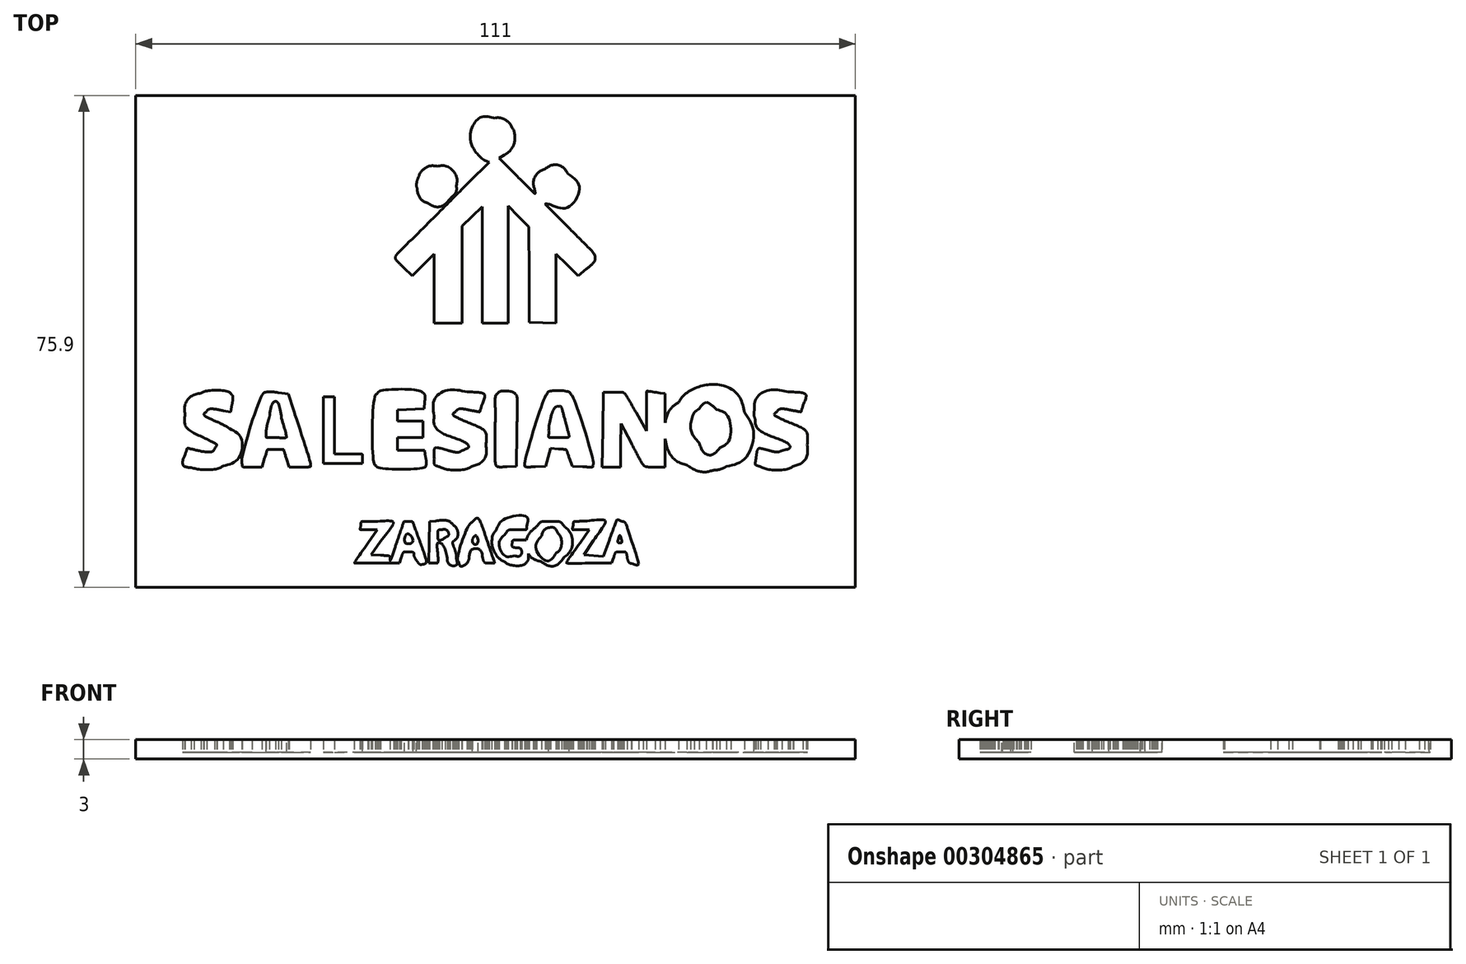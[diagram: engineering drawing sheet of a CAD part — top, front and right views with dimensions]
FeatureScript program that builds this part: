
annotation { "Feature Type Name" : "Feature", "Feature Type Description" : "" }
export const myFeature = defineFeature(function(context is Context, id is Id, definition is map)
    precondition{}
    {
        {
            var Q0;
            Q0=qCreatedBy(makeId("Top.planeOp"),FACE);
            var sketch = newSketch(context, id + "F0", { "sketchPlane" : qUnion([Q0])});
            skFitSpline(sketch, "E0", {"points": [v(-12.14, -33.88) * mm, v(-12.39, -33.52) * mm, v(-12.6, -33.06) * mm, v(-12.6, -32.86) * mm]});
            skFitSpline(sketch, "E1", {"points": [v(-12.6, -32.86) * mm, v(-12.6, -32.65) * mm, v(-12.94, -32.5) * mm, v(-13.42, -32.5) * mm]});
            skFitSpline(sketch, "E2", {"points": [v(-13.42, -32.5) * mm, v(-14.08, -32.5) * mm, v(-14.3, -32.67) * mm, v(-14.54, -33.36) * mm]});
            skLineSegment(sketch, "E3", {"start": v(-14.54, -33.36) * mm, "end": v(-14.84, -34.2) * mm});
            skLineSegment(sketch, "E4", {"start": v(-14.84, -34.2) * mm, "end": v(-17.99, -34.2) * mm});
            skFitSpline(sketch, "E5", {"points": [v(-17.99, -34.2) * mm, v(-21.78, -34.2) * mm, v(-21.79, -34.2) * mm, v(-19.7, -31.17) * mm]});
            skLineSegment(sketch, "E6", {"start": v(-19.7, -31.17) * mm, "end": v(-18.25, -29.08) * mm});
            skLineSegment(sketch, "E7", {"start": v(-18.25, -29.08) * mm, "end": v(-19.57, -29.08) * mm});
            skFitSpline(sketch, "E8", {"points": [v(-19.57, -29.08) * mm, v(-20.78, -29.08) * mm, v(-20.88, -29.03) * mm, v(-20.8, -28.44) * mm]});
            skFitSpline(sketch, "E9", {"points": [v(-20.8, -28.44) * mm, v(-20.71, -27.84) * mm, v(-20.57, -27.8) * mm, v(-18.58, -27.8) * mm]});
            skFitSpline(sketch, "E10", {"points": [v(-18.58, -27.8) * mm, v(-15.85, -27.8) * mm, v(-15.76, -28.1) * mm, v(-17.71, -30.86) * mm]});
            skLineSegment(sketch, "E11", {"start": v(-17.71, -30.86) * mm, "end": v(-19.17, -32.93) * mm});
            skLineSegment(sketch, "E12", {"start": v(-19.17, -32.93) * mm, "end": v(-17.73, -33.01) * mm});
            skFitSpline(sketch, "E13", {"points": [v(-17.73, -33.01) * mm, v(-16.6, -33.08) * mm, v(-16.3, -33.2) * mm, v(-16.29, -33.58) * mm]});
            skFitSpline(sketch, "E14", {"points": [v(-16.29, -33.58) * mm, v(-16.28, -33.85) * mm, v(-15.8, -32.66) * mm, v(-15.22, -30.93) * mm]});
            skFitSpline(sketch, "E15", {"points": [v(-15.22, -30.93) * mm, v(-14.27, -28.12) * mm, v(-14.1, -27.8) * mm, v(-13.48, -27.8) * mm]});
            skFitSpline(sketch, "E16", {"points": [v(-13.48, -27.8) * mm, v(-12.88, -27.8) * mm, v(-12.68, -28.12) * mm, v(-11.83, -30.49) * mm]});
            skFitSpline(sketch, "E17", {"points": [v(-11.83, -30.49) * mm, v(-10.86, -33.17) * mm, v(-10.73, -34.21) * mm, v(-11.36, -34.42) * mm]});
            skFitSpline(sketch, "E18", {"points": [v(-11.36, -34.42) * mm, v(-11.54, -34.48) * mm, v(-11.89, -34.23) * mm, v(-12.14, -33.88) * mm]});
            skFitSpline(sketch, "E19", {"points": [v(-13.8, -31.74) * mm, v(-14, -31.82) * mm, v(-13.84, -31.89) * mm, v(-13.45, -31.89) * mm]});
            skFitSpline(sketch, "E20", {"points": [v(-13.45, -31.89) * mm, v(-13.06, -31.89) * mm, v(-12.9, -31.82) * mm, v(-13.1, -31.74) * mm]});
            skFitSpline(sketch, "E21", {"points": [v(-13.73, -30.65) * mm, v(-13.73, -30.88) * mm, v(-13.6, -31.08) * mm, v(-13.46, -31.08) * mm]});
            skFitSpline(sketch, "E22", {"points": [v(-13.46, -31.08) * mm, v(-13.3, -31.08) * mm, v(-13.25, -30.88) * mm, v(-13.34, -30.65) * mm]});
            skFitSpline(sketch, "E23", {"points": [v(-5.66, -34.05) * mm, v(-5.86, -33.53) * mm, v(-4.09, -28.33) * mm, v(-3.56, -27.9) * mm]});
            skFitSpline(sketch, "E24", {"points": [v(-3.56, -27.9) * mm, v(-2.83, -27.3) * mm, v(-2.28, -28) * mm, v(-1.3, -30.8) * mm]});
            skFitSpline(sketch, "E25", {"points": [v(-1.3, -30.8) * mm, v(-0.18, -34.06) * mm, v(-0.16, -34.2) * mm, v(-1.03, -34.2) * mm]});
            skFitSpline(sketch, "E26", {"points": [v(-1.03, -34.2) * mm, v(-1.53, -34.2) * mm, v(-1.8, -33.98) * mm, v(-2.01, -33.36) * mm]});
            skFitSpline(sketch, "E27", {"points": [v(-2.01, -33.36) * mm, v(-2.43, -32.16) * mm, v(-3.67, -32.14) * mm, v(-4.08, -33.33) * mm]});
            skFitSpline(sketch, "E28", {"points": [v(-4.08, -33.33) * mm, v(-4.4, -34.23) * mm, v(-5.41, -34.7) * mm, v(-5.66, -34.05) * mm]});
            skFitSpline(sketch, "E29", {"points": [v(-3.4, -31.73) * mm, v(-3.68, -31.8) * mm, v(-3.52, -31.87) * mm, v(-3.05, -31.88) * mm]});
            skFitSpline(sketch, "E30", {"points": [v(-3.05, -31.88) * mm, v(-2.58, -31.88) * mm, v(-2.36, -31.82) * mm, v(-2.55, -31.74) * mm]});
            skLineSegment(sketch, "E31", {"start": v(-2.55, -31.74) * mm, "end": v(-2.55, -31.74) * mm});
            skFitSpline(sketch, "E32", {"points": [v(1.37, -34) * mm, v(0.82, -33.73) * mm, v(0.21, -33.18) * mm, v(0.02, -32.79) * mm]});
            skFitSpline(sketch, "E33", {"points": [v(0.02, -32.79) * mm, v(-0.48, -31.8) * mm, v(-0.43, -29.9) * mm, v(0.1, -29.14) * mm]});
            skFitSpline(sketch, "E34", {"points": [v(0.1, -29.14) * mm, v(1.25, -27.5) * mm, v(4.78, -27.05) * mm, v(4.78, -28.54) * mm]});
            skFitSpline(sketch, "E35", {"points": [v(4.78, -28.54) * mm, v(4.78, -29) * mm, v(4.56, -29.08) * mm, v(3.37, -29.08) * mm]});
            skFitSpline(sketch, "E36", {"points": [v(3.37, -29.08) * mm, v(2.24, -29.08) * mm, v(1.88, -29.2) * mm, v(1.52, -29.72) * mm]});
            skFitSpline(sketch, "E37", {"points": [v(1.52, -29.72) * mm, v(0.55, -31.1) * mm, v(1.38, -33.07) * mm, v(2.93, -33.07) * mm]});
            skFitSpline(sketch, "E38", {"points": [v(2.93, -33.07) * mm, v(3.83, -33.07) * mm, v(3.93, -32.07) * mm, v(3.05, -31.84) * mm]});
            skFitSpline(sketch, "E39", {"points": [v(3.05, -31.84) * mm, v(2.66, -31.74) * mm, v(2.49, -31.5) * mm, v(2.55, -31.17) * mm]});
            skFitSpline(sketch, "E40", {"points": [v(2.55, -31.17) * mm, v(2.63, -30.77) * mm, v(2.92, -30.65) * mm, v(3.79, -30.65) * mm]});
            skLineSegment(sketch, "E41", {"start": v(3.79, -30.65) * mm, "end": v(4.92, -30.65) * mm});
            skLineSegment(sketch, "E42", {"start": v(4.92, -30.65) * mm, "end": v(5, -32.19) * mm});
            skFitSpline(sketch, "E43", {"points": [v(5, -32.19) * mm, v(5.06, -33.03) * mm, v(5, -33.82) * mm, v(4.87, -33.95) * mm]});
            skFitSpline(sketch, "E44", {"points": [v(4.87, -33.95) * mm, v(4.33, -34.49) * mm, v(2.36, -34.52) * mm, v(1.37, -34) * mm]});
            skFitSpline(sketch, "E45", {"points": [v(0.41, -30.72) * mm, v(0.33, -30.52) * mm, v(0.27, -30.69) * mm, v(0.27, -31.08) * mm]});
            skFitSpline(sketch, "E46", {"points": [v(0.27, -31.08) * mm, v(0.27, -31.47) * mm, v(0.33, -31.63) * mm, v(0.41, -31.43) * mm]});
            skFitSpline(sketch, "E47", {"points": [v(3.43, -28.33) * mm, v(3.23, -28.25) * mm, v(2.91, -28.25) * mm, v(2.72, -28.33) * mm]});
            skFitSpline(sketch, "E48", {"points": [v(2.72, -28.33) * mm, v(2.52, -28.4) * mm, v(2.68, -28.47) * mm, v(3.07, -28.47) * mm]});
            skFitSpline(sketch, "E49", {"points": [v(7.07, -34) * mm, v(5.23, -33.06) * mm, v(4.85, -30.3) * mm, v(6.33, -28.59) * mm]});
            skFitSpline(sketch, "E50", {"points": [v(6.33, -28.59) * mm, v(6.9, -27.92) * mm, v(7.23, -27.8) * mm, v(8.48, -27.8) * mm]});
            skFitSpline(sketch, "E51", {"points": [v(8.48, -27.8) * mm, v(9.74, -27.8) * mm, v(10.05, -27.92) * mm, v(10.64, -28.6) * mm]});
            skFitSpline(sketch, "E52", {"points": [v(10.64, -28.6) * mm, v(11.67, -29.8) * mm, v(11.63, -32.17) * mm, v(10.55, -33.35) * mm]});
            skFitSpline(sketch, "E53", {"points": [v(10.55, -33.35) * mm, v(9.55, -34.45) * mm, v(8.36, -34.67) * mm, v(7.07, -34) * mm]});
            skFitSpline(sketch, "E54", {"points": [v(9.39, -32.6) * mm, v(10, -32.04) * mm, v(10.09, -30.3) * mm, v(9.54, -29.54) * mm]});
            skFitSpline(sketch, "E55", {"points": [v(9.54, -29.54) * mm, v(8.96, -28.76) * mm, v(7.58, -29.04) * mm, v(7.1, -30.03) * mm]});
            skFitSpline(sketch, "E56", {"points": [v(7.1, -30.03) * mm, v(6.2, -31.92) * mm, v(7.96, -33.9) * mm, v(9.39, -32.6) * mm]});
            skFitSpline(sketch, "E57", {"points": [v(8.14, -28.32) * mm, v(7.92, -28.41) * mm, v(7.98, -28.48) * mm, v(8.32, -28.5) * mm]});
            skFitSpline(sketch, "E58", {"points": [v(8.32, -28.5) * mm, v(8.62, -28.5) * mm, v(8.78, -28.44) * mm, v(8.69, -28.34) * mm]});
            skLineSegment(sketch, "E59", {"start": v(8.69, -28.34) * mm, "end": v(8.69, -28.34) * mm});
            skFitSpline(sketch, "E60", {"points": [v(20.96, -34.29) * mm, v(20.7, -34.22) * mm, v(20.4, -33.8) * mm, v(20.3, -33.34) * mm]});
            skFitSpline(sketch, "E61", {"points": [v(20.3, -33.34) * mm, v(20.15, -32.65) * mm, v(19.97, -32.5) * mm, v(19.3, -32.5) * mm]});
            skFitSpline(sketch, "E62", {"points": [v(19.3, -32.5) * mm, v(18.67, -32.5) * mm, v(18.44, -32.68) * mm, v(18.2, -33.36) * mm]});
            skLineSegment(sketch, "E63", {"start": v(18.2, -33.36) * mm, "end": v(17.9, -34.2) * mm});
            skLineSegment(sketch, "E64", {"start": v(17.9, -34.2) * mm, "end": v(14.76, -34.2) * mm});
            skFitSpline(sketch, "E65", {"points": [v(14.76, -34.2) * mm, v(10.96, -34.2) * mm, v(10.92, -34.14) * mm, v(13.05, -31.12) * mm]});
            skLineSegment(sketch, "E66", {"start": v(13.05, -31.12) * mm, "end": v(14.48, -29.08) * mm});
            skLineSegment(sketch, "E67", {"start": v(14.48, -29.08) * mm, "end": v(13.17, -29.08) * mm});
            skFitSpline(sketch, "E68", {"points": [v(13.17, -29.08) * mm, v(11.97, -29.08) * mm, v(11.87, -29.03) * mm, v(11.95, -28.44) * mm]});
            skFitSpline(sketch, "E69", {"points": [v(11.95, -28.44) * mm, v(12.03, -27.85) * mm, v(12.21, -27.8) * mm, v(14.11, -27.72) * mm]});
            skFitSpline(sketch, "E70", {"points": [v(14.11, -27.72) * mm, v(16.85, -27.6) * mm, v(16.94, -27.9) * mm, v(15.07, -30.73) * mm]});
            skLineSegment(sketch, "E71", {"start": v(15.07, -30.73) * mm, "end": v(13.61, -32.93) * mm});
            skLineSegment(sketch, "E72", {"start": v(13.61, -32.93) * mm, "end": v(15.1, -33.07) * mm});
            skLineSegment(sketch, "E73", {"start": v(15.1, -33.07) * mm, "end": v(16.6, -33.21) * mm});
            skLineSegment(sketch, "E74", {"start": v(16.6, -33.21) * mm, "end": v(17.54, -30.65) * mm});
            skFitSpline(sketch, "E75", {"points": [v(17.54, -30.65) * mm, v(18.6, -27.75) * mm, v(18.75, -27.53) * mm, v(19.5, -27.77) * mm]});
            skFitSpline(sketch, "E76", {"points": [v(19.5, -27.77) * mm, v(19.9, -27.9) * mm, v(20.31, -28.77) * mm, v(21.01, -30.94) * mm]});
            skFitSpline(sketch, "E77", {"points": [v(21.01, -30.94) * mm, v(21.98, -33.92) * mm, v(21.97, -34.52) * mm, v(20.96, -34.29) * mm]});
            skFitSpline(sketch, "E78", {"points": [v(18.81, -31.73) * mm, v(18.53, -31.8) * mm, v(18.7, -31.87) * mm, v(19.16, -31.88) * mm]});
            skFitSpline(sketch, "E79", {"points": [v(19.16, -31.88) * mm, v(19.63, -31.88) * mm, v(19.86, -31.82) * mm, v(19.67, -31.74) * mm]});
            skLineSegment(sketch, "E80", {"start": v(19.67, -31.74) * mm, "end": v(19.67, -31.74) * mm});
            skFitSpline(sketch, "E81", {"points": [v(19.39, -30.5) * mm, v(19.3, -30.2) * mm, v(19.2, -29.94) * mm, v(19.16, -29.94) * mm]});
            skFitSpline(sketch, "E82", {"points": [v(19.16, -29.94) * mm, v(19.12, -29.94) * mm, v(19.02, -30.2) * mm, v(18.94, -30.5) * mm]});
            skFitSpline(sketch, "E83", {"points": [v(18.94, -30.5) * mm, v(18.84, -30.86) * mm, v(18.93, -31.08) * mm, v(19.16, -31.08) * mm]});
            skFitSpline(sketch, "E84", {"points": [v(19.16, -31.08) * mm, v(19.4, -31.08) * mm, v(19.48, -30.86) * mm, v(19.39, -30.5) * mm]});
            skLineSegment(sketch, "E85", {"start": v(-10.25, -31) * mm, "end": v(-10.17, -27.8) * mm});
            skLineSegment(sketch, "E86", {"start": v(-10.17, -27.8) * mm, "end": v(-9.2, -27.7) * mm});
            skFitSpline(sketch, "E87", {"points": [v(-9.2, -27.7) * mm, v(-7.98, -27.6) * mm, v(-7.06, -27.82) * mm, v(-6.49, -28.4) * mm]});
            skFitSpline(sketch, "E88", {"points": [v(-6.49, -28.4) * mm, v(-5.97, -28.91) * mm, v(-5.9, -30.25) * mm, v(-6.36, -30.71) * mm]});
            skFitSpline(sketch, "E89", {"points": [v(-6.36, -30.71) * mm, v(-6.6, -30.95) * mm, v(-6.6, -31.27) * mm, v(-6.36, -31.95) * mm]});
            skFitSpline(sketch, "E90", {"points": [v(-6.36, -31.95) * mm, v(-6.19, -32.46) * mm, v(-6.04, -33.17) * mm, v(-6.04, -33.54) * mm]});
            skFitSpline(sketch, "E91", {"points": [v(-6.04, -33.54) * mm, v(-6.04, -34.53) * mm, v(-7.11, -34.44) * mm, v(-7.47, -33.43) * mm]});
            skFitSpline(sketch, "E92", {"points": [v(-7.47, -33.43) * mm, v(-8.21, -31.35) * mm, v(-8.9, -31.1) * mm, v(-8.9, -32.9) * mm]});
            skFitSpline(sketch, "E93", {"points": [v(-8.9, -32.9) * mm, v(-8.9, -34.11) * mm, v(-8.94, -34.2) * mm, v(-9.61, -34.2) * mm]});
            skLineSegment(sketch, "E94", {"start": v(-9.61, -34.2) * mm, "end": v(-10.33, -34.2) * mm});
            skLineSegment(sketch, "E95", {"start": v(-10.33, -34.2) * mm, "end": v(-10.25, -31) * mm});
            skFitSpline(sketch, "E96", {"points": [v(-9.54, -32.15) * mm, v(-9.61, -31.8) * mm, v(-9.67, -32.02) * mm, v(-9.67, -32.64) * mm]});
            skFitSpline(sketch, "E97", {"points": [v(-9.67, -32.64) * mm, v(-9.68, -33.27) * mm, v(-9.62, -33.56) * mm, v(-9.55, -33.29) * mm]});
            skFitSpline(sketch, "E98", {"points": [v(-9.54, -29.3) * mm, v(-9.61, -28.95) * mm, v(-9.67, -29.17) * mm, v(-9.67, -29.8) * mm]});
            skFitSpline(sketch, "E99", {"points": [v(-9.67, -29.8) * mm, v(-9.68, -30.42) * mm, v(-9.62, -30.71) * mm, v(-9.55, -30.44) * mm]});
            skFitSpline(sketch, "E100", {"points": [v(-7.78, -30.25) * mm, v(-7.23, -29.9) * mm, v(-7.6, -29.08) * mm, v(-8.31, -29.08) * mm]});
            skFitSpline(sketch, "E101", {"points": [v(-8.31, -29.08) * mm, v(-8.74, -29.08) * mm, v(-8.9, -29.27) * mm, v(-8.9, -29.8) * mm]});
            skFitSpline(sketch, "E102", {"points": [v(-8.9, -29.8) * mm, v(-8.9, -30.53) * mm, v(-8.48, -30.7) * mm, v(-7.78, -30.25) * mm]});
            skFitSpline(sketch, "E103", {"points": [v(-8.25, -28.33) * mm, v(-8.45, -28.25) * mm, v(-8.77, -28.25) * mm, v(-8.96, -28.33) * mm]});
            skFitSpline(sketch, "E104", {"points": [v(-8.96, -28.33) * mm, v(-9.16, -28.4) * mm, v(-9, -28.47) * mm, v(-8.6, -28.47) * mm]});
            skFitSpline(sketch, "E105", {"points": [v(-46.96, -19.49) * mm, v(-48.01, -19.28) * mm, v(-48.29, -18.7) * mm, v(-47.9, -17.53) * mm]});
            skFitSpline(sketch, "E106", {"points": [v(-47.9, -17.53) * mm, v(-47.57, -16.52) * mm, v(-47.52, -16.5) * mm, v(-46.52, -16.7) * mm]});
            skFitSpline(sketch, "E107", {"points": [v(-46.52, -16.7) * mm, v(-44.91, -17.04) * mm, v(-43.6, -16.97) * mm, v(-43.34, -16.54) * mm]});
            skFitSpline(sketch, "E108", {"points": [v(-43.34, -16.54) * mm, v(-43, -15.98) * mm, v(-43.2, -15.78) * mm, v(-45.05, -14.85) * mm]});
            skFitSpline(sketch, "E109", {"points": [v(-45.05, -14.85) * mm, v(-47.17, -13.78) * mm, v(-47.9, -12.86) * mm, v(-47.9, -11.27) * mm]});
            skFitSpline(sketch, "E110", {"points": [v(-47.9, -11.27) * mm, v(-47.9, -9.77) * mm, v(-46.94, -8.49) * mm, v(-45.43, -8) * mm]});
            skFitSpline(sketch, "E111", {"points": [v(-45.43, -8) * mm, v(-44.3, -7.62) * mm, v(-41.18, -7.78) * mm, v(-40.72, -8.24) * mm]});
            skFitSpline(sketch, "E112", {"points": [v(-40.72, -8.24) * mm, v(-40.56, -8.4) * mm, v(-40.53, -9.02) * mm, v(-40.64, -9.71) * mm]});
            skLineSegment(sketch, "E113", {"start": v(-40.64, -9.71) * mm, "end": v(-40.84, -10.9) * mm});
            skLineSegment(sketch, "E114", {"start": v(-40.84, -10.9) * mm, "end": v(-42.03, -10.69) * mm});
            skFitSpline(sketch, "E115", {"points": [v(-42.03, -10.69) * mm, v(-43.5, -10.43) * mm, v(-44.21, -10.46) * mm, v(-44.56, -10.82) * mm]});
            skFitSpline(sketch, "E116", {"points": [v(-44.56, -10.82) * mm, v(-45, -11.25) * mm, v(-44.56, -11.69) * mm, v(-42.97, -12.42) * mm]});
            skFitSpline(sketch, "E117", {"points": [v(-42.97, -12.42) * mm, v(-42.16, -12.8) * mm, v(-41.3, -13.27) * mm, v(-41.05, -13.47) * mm]});
            skFitSpline(sketch, "E118", {"points": [v(-41.05, -13.47) * mm, v(-39.21, -14.98) * mm, v(-39.74, -18.14) * mm, v(-42, -19.2) * mm]});
            skFitSpline(sketch, "E119", {"points": [v(-42, -19.2) * mm, v(-42.95, -19.66) * mm, v(-45.38, -19.8) * mm, v(-46.96, -19.49) * mm]});
            skFitSpline(sketch, "E120", {"points": [v(-42.21, -18.32) * mm, v(-41.17, -17.67) * mm, v(-40.8, -17.1) * mm, v(-40.8, -16.08) * mm]});
            skFitSpline(sketch, "E121", {"points": [v(-40.8, -16.08) * mm, v(-40.78, -14.88) * mm, v(-41.87, -13.62) * mm, v(-43.32, -13.14) * mm]});
            skFitSpline(sketch, "E122", {"points": [v(-43.32, -13.14) * mm, v(-45.42, -12.45) * mm, v(-46.2, -11.18) * mm, v(-45.15, -10.13) * mm]});
            skFitSpline(sketch, "E123", {"points": [v(-45.15, -10.13) * mm, v(-44.78, -9.76) * mm, v(-44.3, -9.68) * mm, v(-43.01, -9.78) * mm]});
            skFitSpline(sketch, "E124", {"points": [v(-43.01, -9.78) * mm, v(-41.58, -9.88) * mm, v(-41.36, -9.83) * mm, v(-41.36, -9.4) * mm]});
            skFitSpline(sketch, "E125", {"points": [v(-41.36, -9.4) * mm, v(-41.36, -8) * mm, v(-45.5, -8.33) * mm, v(-46.74, -9.83) * mm]});
            skFitSpline(sketch, "E126", {"points": [v(-46.74, -9.83) * mm, v(-47.28, -10.48) * mm, v(-47.2, -12.22) * mm, v(-46.58, -12.9) * mm]});
            skFitSpline(sketch, "E127", {"points": [v(-46.58, -12.9) * mm, v(-46.3, -13.22) * mm, v(-45.35, -13.8) * mm, v(-44.5, -14.18) * mm]});
            skFitSpline(sketch, "E128", {"points": [v(-44.5, -14.18) * mm, v(-42.76, -14.95) * mm, v(-42.5, -15.22) * mm, v(-42.5, -16.33) * mm]});
            skFitSpline(sketch, "E129", {"points": [v(-42.5, -16.33) * mm, v(-42.5, -17.4) * mm, v(-43.35, -17.8) * mm, v(-45.36, -17.61) * mm]});
            skFitSpline(sketch, "E130", {"points": [v(-45.36, -17.61) * mm, v(-46.8, -17.48) * mm, v(-47.02, -17.53) * mm, v(-47.14, -18) * mm]});
            skFitSpline(sketch, "E131", {"points": [v(-47.14, -18) * mm, v(-47.24, -18.4) * mm, v(-47.1, -18.59) * mm, v(-46.67, -18.68) * mm]});
            skFitSpline(sketch, "E132", {"points": [v(-46.67, -18.68) * mm, v(-46.33, -18.75) * mm, v(-45.8, -18.86) * mm, v(-45.49, -18.93) * mm]});
            skFitSpline(sketch, "E133", {"points": [v(-45.49, -18.93) * mm, v(-44.6, -19.11) * mm, v(-43, -18.82) * mm, v(-42.21, -18.32) * mm]});
            skFitSpline(sketch, "E134", {"points": [v(-8.68, -19.35) * mm, v(-9.3, -19.12) * mm, v(-9.46, -18.9) * mm, v(-9.46, -18.17) * mm]});
            skFitSpline(sketch, "E135", {"points": [v(-9.46, -18.17) * mm, v(-9.45, -16.59) * mm, v(-9.16, -16.4) * mm, v(-7.4, -16.82) * mm]});
            skFitSpline(sketch, "E136", {"points": [v(-7.4, -16.82) * mm, v(-6.21, -17.1) * mm, v(-5.7, -17.11) * mm, v(-5.23, -16.86) * mm]});
            skFitSpline(sketch, "E137", {"points": [v(-5.23, -16.86) * mm, v(-4.14, -16.28) * mm, v(-4.51, -15.71) * mm, v(-6.55, -14.84) * mm]});
            skFitSpline(sketch, "E138", {"points": [v(-6.55, -14.84) * mm, v(-8.46, -14.02) * mm, v(-9.46, -12.87) * mm, v(-9.46, -11.48) * mm]});
            skFitSpline(sketch, "E139", {"points": [v(-9.46, -11.48) * mm, v(-9.46, -9) * mm, v(-7.46, -7.55) * mm, v(-4.4, -7.8) * mm]});
            skFitSpline(sketch, "E140", {"points": [v(-4.4, -7.8) * mm, v(-2.08, -7.99) * mm, v(-1.67, -8.35) * mm, v(-2.11, -9.8) * mm]});
            skFitSpline(sketch, "E141", {"points": [v(-2.11, -9.8) * mm, v(-2.44, -10.88) * mm, v(-2.45, -10.89) * mm, v(-3.6, -10.68) * mm]});
            skFitSpline(sketch, "E142", {"points": [v(-3.6, -10.68) * mm, v(-5.05, -10.43) * mm, v(-5.77, -10.47) * mm, v(-6.12, -10.82) * mm]});
            skFitSpline(sketch, "E143", {"points": [v(-6.12, -10.82) * mm, v(-6.56, -11.26) * mm, v(-6.1, -11.68) * mm, v(-4.21, -12.54) * mm]});
            skFitSpline(sketch, "E144", {"points": [v(-4.21, -12.54) * mm, v(-2.06, -13.51) * mm, v(-1.49, -14.24) * mm, v(-1.49, -16) * mm]});
            skFitSpline(sketch, "E145", {"points": [v(-1.49, -16) * mm, v(-1.49, -17.57) * mm, v(-2.23, -18.7) * mm, v(-3.66, -19.3) * mm]});
            skFitSpline(sketch, "E146", {"points": [v(-3.66, -19.3) * mm, v(-4.74, -19.74) * mm, v(-7.52, -19.78) * mm, v(-8.68, -19.35) * mm]});
            skFitSpline(sketch, "E147", {"points": [v(-3.67, -18.35) * mm, v(-2.64, -17.82) * mm, v(-2.04, -16.45) * mm, v(-2.36, -15.33) * mm]});
            skFitSpline(sketch, "E148", {"points": [v(-2.36, -15.33) * mm, v(-2.65, -14.32) * mm, v(-3.12, -13.94) * mm, v(-5.26, -12.95) * mm]});
            skFitSpline(sketch, "E149", {"points": [v(-5.26, -12.95) * mm, v(-6.76, -12.27) * mm, v(-6.9, -12.13) * mm, v(-6.9, -11.28) * mm]});
            skFitSpline(sketch, "E150", {"points": [v(-6.9, -11.28) * mm, v(-6.9, -9.98) * mm, v(-6.33, -9.62) * mm, v(-4.5, -9.78) * mm]});
            skFitSpline(sketch, "E151", {"points": [v(-4.5, -9.78) * mm, v(-3.19, -9.88) * mm, v(-2.93, -9.83) * mm, v(-2.82, -9.4) * mm]});
            skFitSpline(sketch, "E152", {"points": [v(-2.82, -9.4) * mm, v(-2.65, -8.77) * mm, v(-3.3, -8.53) * mm, v(-5.07, -8.53) * mm]});
            skFitSpline(sketch, "E153", {"points": [v(-5.07, -8.53) * mm, v(-7.11, -8.53) * mm, v(-8.58, -9.71) * mm, v(-8.6, -11.37) * mm]});
            skFitSpline(sketch, "E154", {"points": [v(-8.6, -11.37) * mm, v(-8.6, -12.55) * mm, v(-7.75, -13.44) * mm, v(-5.77, -14.3) * mm]});
            skFitSpline(sketch, "E155", {"points": [v(-5.77, -14.3) * mm, v(-4, -15.06) * mm, v(-3.5, -15.95) * mm, v(-4.21, -17.05) * mm]});
            skFitSpline(sketch, "E156", {"points": [v(-4.21, -17.05) * mm, v(-4.65, -17.72) * mm, v(-4.8, -17.76) * mm, v(-6.62, -17.63) * mm]});
            skFitSpline(sketch, "E157", {"points": [v(-6.62, -17.63) * mm, v(-8.32, -17.5) * mm, v(-8.58, -17.55) * mm, v(-8.7, -18) * mm]});
            skFitSpline(sketch, "E158", {"points": [v(-8.7, -18) * mm, v(-8.97, -19.05) * mm, v(-5.52, -19.28) * mm, v(-3.67, -18.35) * mm]});
            skFitSpline(sketch, "E159", {"points": [v(30.83, -19.29) * mm, v(27.06, -17.64) * mm, v(26.6, -11.02) * mm, v(30.1, -8.7) * mm]});
            skFitSpline(sketch, "E160", {"points": [v(30.1, -8.7) * mm, v(33.07, -6.74) * mm, v(36.98, -7.82) * mm, v(38.42, -11) * mm]});
            skFitSpline(sketch, "E161", {"points": [v(38.42, -11) * mm, v(39.79, -14) * mm, v(38.39, -18.15) * mm, v(35.62, -19.3) * mm]});
            skFitSpline(sketch, "E162", {"points": [v(35.62, -19.3) * mm, v(34.46, -19.79) * mm, v(31.96, -19.78) * mm, v(30.83, -19.29) * mm]});
            skFitSpline(sketch, "E163", {"points": [v(35.58, -18.38) * mm, v(38.12, -17.07) * mm, v(38.95, -12.53) * mm, v(37.05, -10.28) * mm]});
            skFitSpline(sketch, "E164", {"points": [v(37.05, -10.28) * mm, v(34.1, -6.77) * mm, v(28.55, -8.9) * mm, v(28.44, -13.56) * mm]});
            skFitSpline(sketch, "E165", {"points": [v(28.44, -13.56) * mm, v(28.34, -17.63) * mm, v(32.12, -20.17) * mm, v(35.58, -18.38) * mm]});
            skFitSpline(sketch, "E166", {"points": [v(31.17, -16.84) * mm, v(29.77, -15.18) * mm, v(29.9, -11.9) * mm, v(31.42, -10.4) * mm]});
            skFitSpline(sketch, "E167", {"points": [v(31.42, -10.4) * mm, v(32.35, -9.46) * mm, v(34.33, -9.44) * mm, v(35.18, -10.36) * mm]});
            skFitSpline(sketch, "E168", {"points": [v(35.18, -10.36) * mm, v(35.98, -11.2) * mm, v(36.4, -12.35) * mm, v(36.4, -13.7) * mm]});
            skFitSpline(sketch, "E169", {"points": [v(36.4, -13.7) * mm, v(36.4, -15.06) * mm, v(35.98, -16.2) * mm, v(35.18, -17.05) * mm]});
            skFitSpline(sketch, "E170", {"points": [v(35.18, -17.05) * mm, v(34.72, -17.54) * mm, v(34.27, -17.7) * mm, v(33.23, -17.7) * mm]});
            skFitSpline(sketch, "E171", {"points": [v(33.23, -17.7) * mm, v(32.08, -17.7) * mm, v(31.78, -17.57) * mm, v(31.17, -16.84) * mm]});
            skFitSpline(sketch, "E172", {"points": [v(34.57, -16.46) * mm, v(36.06, -15.18) * mm, v(35.75, -11.45) * mm, v(34.08, -10.56) * mm]});
            skFitSpline(sketch, "E173", {"points": [v(34.08, -10.56) * mm, v(31.99, -9.43) * mm, v(30.07, -13.11) * mm, v(31.4, -15.7) * mm]});
            skFitSpline(sketch, "E174", {"points": [v(31.4, -15.7) * mm, v(32.2, -17.23) * mm, v(33.35, -17.5) * mm, v(34.57, -16.46) * mm]});
            skFitSpline(sketch, "E175", {"points": [v(40.84, -19.34) * mm, v(40.1, -19.07) * mm, v(40.04, -18.96) * mm, v(40.18, -17.92) * mm]});
            skFitSpline(sketch, "E176", {"points": [v(40.18, -17.92) * mm, v(40.26, -17.3) * mm, v(40.4, -16.71) * mm, v(40.5, -16.62) * mm]});
            skFitSpline(sketch, "E177", {"points": [v(40.5, -16.62) * mm, v(40.6, -16.52) * mm, v(41.29, -16.6) * mm, v(42.04, -16.8) * mm]});
            skFitSpline(sketch, "E178", {"points": [v(42.04, -16.8) * mm, v(43, -17.05) * mm, v(43.63, -17.06) * mm, v(44.17, -16.86) * mm]});
            skFitSpline(sketch, "E179", {"points": [v(44.17, -16.86) * mm, v(45.4, -16.39) * mm, v(45.09, -15.77) * mm, v(43.14, -14.89) * mm]});
            skFitSpline(sketch, "E180", {"points": [v(43.14, -14.89) * mm, v(41, -13.92) * mm, v(40.1, -12.9) * mm, v(40.1, -11.46) * mm]});
            skFitSpline(sketch, "E181", {"points": [v(40.1, -11.46) * mm, v(40.1, -9) * mm, v(42.1, -7.56) * mm, v(45.15, -7.8) * mm]});
            skFitSpline(sketch, "E182", {"points": [v(45.15, -7.8) * mm, v(47.48, -7.99) * mm, v(47.89, -8.35) * mm, v(47.44, -9.8) * mm]});
            skFitSpline(sketch, "E183", {"points": [v(47.44, -9.8) * mm, v(47.11, -10.88) * mm, v(47.1, -10.89) * mm, v(45.95, -10.68) * mm]});
            skFitSpline(sketch, "E184", {"points": [v(45.95, -10.68) * mm, v(44.5, -10.43) * mm, v(43.79, -10.47) * mm, v(43.44, -10.82) * mm]});
            skFitSpline(sketch, "E185", {"points": [v(43.44, -10.82) * mm, v(42.99, -11.26) * mm, v(43.45, -11.68) * mm, v(45.34, -12.54) * mm]});
            skFitSpline(sketch, "E186", {"points": [v(45.34, -12.54) * mm, v(47.5, -13.51) * mm, v(48.07, -14.24) * mm, v(48.07, -16) * mm]});
            skFitSpline(sketch, "E187", {"points": [v(48.07, -16) * mm, v(48.07, -17.57) * mm, v(47.32, -18.7) * mm, v(45.9, -19.3) * mm]});
            skFitSpline(sketch, "E188", {"points": [v(45.9, -19.3) * mm, v(44.8, -19.75) * mm, v(42.03, -19.78) * mm, v(40.84, -19.34) * mm]});
            skFitSpline(sketch, "E189", {"points": [v(45.85, -18.36) * mm, v(46.83, -17.87) * mm, v(47.21, -17.16) * mm, v(47.21, -15.86) * mm]});
            skFitSpline(sketch, "E190", {"points": [v(47.21, -15.86) * mm, v(47.21, -14.66) * mm, v(46.53, -13.96) * mm, v(44.3, -12.86) * mm]});
            skFitSpline(sketch, "E191", {"points": [v(44.3, -12.86) * mm, v(42.42, -11.94) * mm, v(42.1, -11.44) * mm, v(42.78, -10.43) * mm]});
            skFitSpline(sketch, "E192", {"points": [v(42.78, -10.43) * mm, v(43.25, -9.7) * mm, v(43.39, -9.66) * mm, v(44.94, -9.77) * mm]});
            skFitSpline(sketch, "E193", {"points": [v(44.94, -9.77) * mm, v(46.36, -9.88) * mm, v(46.63, -9.82) * mm, v(46.74, -9.39) * mm]});
            skFitSpline(sketch, "E194", {"points": [v(46.74, -9.39) * mm, v(47, -8.35) * mm, v(43.8, -8.17) * mm, v(42.26, -9.13) * mm]});
            skFitSpline(sketch, "E195", {"points": [v(42.26, -9.13) * mm, v(39.94, -10.56) * mm, v(40.5, -12.69) * mm, v(43.58, -14.2) * mm]});
            skFitSpline(sketch, "E196", {"points": [v(43.58, -14.2) * mm, v(45.39, -15.08) * mm, v(45.5, -15.2) * mm, v(45.5, -16.1) * mm]});
            skFitSpline(sketch, "E197", {"points": [v(45.5, -16.1) * mm, v(45.5, -17.49) * mm, v(44.97, -17.8) * mm, v(42.82, -17.62) * mm]});
            skFitSpline(sketch, "E198", {"points": [v(42.82, -17.62) * mm, v(41.22, -17.5) * mm, v(40.98, -17.54) * mm, v(40.86, -18) * mm]});
            skFitSpline(sketch, "E199", {"points": [v(40.86, -18) * mm, v(40.59, -19.04) * mm, v(44.02, -19.29) * mm, v(45.85, -18.36) * mm]});
            skFitSpline(sketch, "E200", {"points": [v(-39.08, -18.96) * mm, v(-39.08, -17.94) * mm, v(-35.83, -8.03) * mm, v(-35.45, -7.88) * mm]});
            skFitSpline(sketch, "E201", {"points": [v(-35.45, -7.88) * mm, v(-35.23, -7.8) * mm, v(-34.36, -7.8) * mm, v(-33.51, -7.9) * mm]});
            skLineSegment(sketch, "E202", {"start": v(-33.51, -7.9) * mm, "end": v(-31.98, -8.08) * mm});
            skLineSegment(sketch, "E203", {"start": v(-31.98, -8.08) * mm, "end": v(-31.13, -10.68) * mm});
            skFitSpline(sketch, "E204", {"points": [v(-31.13, -10.68) * mm, v(-29.98, -14.24) * mm, v(-28.54, -18.96) * mm, v(-28.54, -19.2) * mm]});
            skFitSpline(sketch, "E205", {"points": [v(-28.54, -19.2) * mm, v(-28.54, -19.31) * mm, v(-29.29, -19.4) * mm, v(-30.2, -19.4) * mm]});
            skLineSegment(sketch, "E206", {"start": v(-30.2, -19.4) * mm, "end": v(-31.86, -19.4) * mm});
            skLineSegment(sketch, "E207", {"start": v(-31.86, -19.4) * mm, "end": v(-32.28, -18.05) * mm});
            skFitSpline(sketch, "E208", {"points": [v(-32.28, -18.05) * mm, v(-32.7, -16.7) * mm, v(-32.7, -16.7) * mm, v(-33.95, -16.7) * mm]});
            skFitSpline(sketch, "E209", {"points": [v(-33.95, -16.7) * mm, v(-35.2, -16.7) * mm, v(-35.2, -16.7) * mm, v(-35.62, -18.05) * mm]});
            skLineSegment(sketch, "E210", {"start": v(-35.62, -18.05) * mm, "end": v(-36.04, -19.4) * mm});
            skLineSegment(sketch, "E211", {"start": v(-36.04, -19.4) * mm, "end": v(-37.56, -19.4) * mm});
            skFitSpline(sketch, "E212", {"points": [v(-37.56, -19.4) * mm, v(-38.74, -19.4) * mm, v(-39.08, -19.3) * mm, v(-39.08, -18.96) * mm]});
            skFitSpline(sketch, "E213", {"points": [v(-36.51, -18.47) * mm, v(-36.51, -18.28) * mm, v(-36.38, -17.64) * mm, v(-36.21, -17.05) * mm]});
            skLineSegment(sketch, "E214", {"start": v(-36.21, -17.05) * mm, "end": v(-35.92, -15.98) * mm});
            skLineSegment(sketch, "E215", {"start": v(-35.92, -15.98) * mm, "end": v(-33.95, -15.98) * mm});
            skLineSegment(sketch, "E216", {"start": v(-33.95, -15.98) * mm, "end": v(-32, -15.98) * mm});
            skLineSegment(sketch, "E217", {"start": v(-32, -15.98) * mm, "end": v(-31.61, -17.34) * mm});
            skFitSpline(sketch, "E218", {"points": [v(-31.61, -17.34) * mm, v(-31.27, -18.55) * mm, v(-31.14, -18.7) * mm, v(-30.34, -18.78) * mm]});
            skLineSegment(sketch, "E219", {"start": v(-30.34, -18.78) * mm, "end": v(-29.45, -18.86) * mm});
            skLineSegment(sketch, "E220", {"start": v(-29.45, -18.86) * mm, "end": v(-30.6, -15.22) * mm});
            skFitSpline(sketch, "E221", {"points": [v(-30.6, -15.22) * mm, v(-31.23, -13.2) * mm, v(-31.94, -10.89) * mm, v(-32.19, -10.06) * mm]});
            skLineSegment(sketch, "E222", {"start": v(-32.19, -10.06) * mm, "end": v(-32.63, -8.55) * mm});
            skLineSegment(sketch, "E223", {"start": v(-32.63, -8.55) * mm, "end": v(-33.92, -8.64) * mm});
            skLineSegment(sketch, "E224", {"start": v(-33.92, -8.64) * mm, "end": v(-35.2, -8.72) * mm});
            skLineSegment(sketch, "E225", {"start": v(-35.2, -8.72) * mm, "end": v(-36.56, -13.14) * mm});
            skFitSpline(sketch, "E226", {"points": [v(-36.56, -13.14) * mm, v(-38.46, -19.36) * mm, v(-38.39, -18.83) * mm, v(-37.37, -18.83) * mm]});
            skFitSpline(sketch, "E227", {"points": [v(-37.37, -18.83) * mm, v(-36.88, -18.83) * mm, v(-36.51, -18.68) * mm, v(-36.51, -18.47) * mm]});
            skFitSpline(sketch, "E228", {"points": [v(-35.38, -14.13) * mm, v(-35.38, -13.73) * mm, v(-35.16, -12.64) * mm, v(-34.9, -11.7) * mm]});
            skFitSpline(sketch, "E229", {"points": [v(-34.9, -11.7) * mm, v(-34.25, -9.37) * mm, v(-33.66, -9.4) * mm, v(-33.01, -11.83) * mm]});
            skFitSpline(sketch, "E230", {"points": [v(-33.01, -11.83) * mm, v(-32.24, -14.73) * mm, v(-32.28, -14.84) * mm, v(-33.95, -14.84) * mm]});
            skFitSpline(sketch, "E231", {"points": [v(-33.95, -14.84) * mm, v(-35.28, -14.84) * mm, v(-35.38, -14.8) * mm, v(-35.38, -14.13) * mm]});
            skFitSpline(sketch, "E232", {"points": [v(-33.44, -13.35) * mm, v(-33.9, -11.94) * mm, v(-34.1, -11.9) * mm, v(-34.42, -13.14) * mm]});
            skFitSpline(sketch, "E233", {"points": [v(-34.42, -13.14) * mm, v(-34.72, -14.27) * mm, v(-34.72, -14.27) * mm, v(-33.93, -14.27) * mm]});
            skFitSpline(sketch, "E234", {"points": [v(-33.93, -14.27) * mm, v(-33.15, -14.27) * mm, v(-33.14, -14.25) * mm, v(-33.44, -13.35) * mm]});
            skFitSpline(sketch, "E235", {"points": [v(-27.12, -13.7) * mm, v(-27.12, -7.35) * mm, v(-27.15, -7.46) * mm, v(-25.2, -7.92) * mm]});
            skLineSegment(sketch, "E236", {"start": v(-25.2, -7.92) * mm, "end": v(-24.13, -8.17) * mm});
            skLineSegment(sketch, "E237", {"start": v(-24.13, -8.17) * mm, "end": v(-24.05, -12.5) * mm});
            skLineSegment(sketch, "E238", {"start": v(-24.05, -12.5) * mm, "end": v(-23.97, -16.84) * mm});
            skLineSegment(sketch, "E239", {"start": v(-23.97, -16.84) * mm, "end": v(-21.84, -16.84) * mm});
            skLineSegment(sketch, "E240", {"start": v(-21.84, -16.84) * mm, "end": v(-19.71, -16.84) * mm});
            skLineSegment(sketch, "E241", {"start": v(-19.71, -16.84) * mm, "end": v(-19.71, -18.12) * mm});
            skLineSegment(sketch, "E242", {"start": v(-19.71, -18.12) * mm, "end": v(-19.71, -19.4) * mm});
            skLineSegment(sketch, "E243", {"start": v(-19.71, -19.4) * mm, "end": v(-23.41, -19.4) * mm});
            skLineSegment(sketch, "E244", {"start": v(-23.41, -19.4) * mm, "end": v(-27.12, -19.4) * mm});
            skLineSegment(sketch, "E245", {"start": v(-27.12, -19.4) * mm, "end": v(-27.12, -13.7) * mm});
            skFitSpline(sketch, "E246", {"points": [v(-20.57, -18.12) * mm, v(-20.57, -17.42) * mm, v(-20.61, -17.4) * mm, v(-22.7, -17.4) * mm]});
            skLineSegment(sketch, "E247", {"start": v(-22.7, -17.4) * mm, "end": v(-24.84, -17.4) * mm});
            skLineSegment(sketch, "E248", {"start": v(-24.84, -17.4) * mm, "end": v(-24.84, -13) * mm});
            skLineSegment(sketch, "E249", {"start": v(-24.84, -13) * mm, "end": v(-24.84, -8.58) * mm});
            skLineSegment(sketch, "E250", {"start": v(-24.84, -8.58) * mm, "end": v(-25.7, -8.58) * mm});
            skLineSegment(sketch, "E251", {"start": v(-25.7, -8.58) * mm, "end": v(-26.55, -8.58) * mm});
            skLineSegment(sketch, "E252", {"start": v(-26.55, -8.58) * mm, "end": v(-26.55, -13.7) * mm});
            skLineSegment(sketch, "E253", {"start": v(-26.55, -13.7) * mm, "end": v(-26.55, -18.83) * mm});
            skLineSegment(sketch, "E254", {"start": v(-26.55, -18.83) * mm, "end": v(-23.56, -18.83) * mm});
            skLineSegment(sketch, "E255", {"start": v(-23.56, -18.83) * mm, "end": v(-20.57, -18.83) * mm});
            skLineSegment(sketch, "E256", {"start": v(-20.57, -18.83) * mm, "end": v(-20.57, -18.12) * mm});
            skFitSpline(sketch, "E257", {"points": [v(-18.38, -19.21) * mm, v(-18.74, -18.85) * mm, v(-18.6, -8.43) * mm, v(-18.23, -8.07) * mm]});
            skFitSpline(sketch, "E258", {"points": [v(-18.23, -8.07) * mm, v(-17.83, -7.67) * mm, v(-11.82, -7.59) * mm, v(-11.22, -7.97) * mm]});
            skFitSpline(sketch, "E259", {"points": [v(-11.22, -7.97) * mm, v(-10.98, -8.12) * mm, v(-10.88, -8.62) * mm, v(-10.94, -9.32) * mm]});
            skLineSegment(sketch, "E260", {"start": v(-10.94, -9.32) * mm, "end": v(-11.03, -10.43) * mm});
            skLineSegment(sketch, "E261", {"start": v(-11.03, -10.43) * mm, "end": v(-13.1, -10.51) * mm});
            skLineSegment(sketch, "E262", {"start": v(-13.1, -10.51) * mm, "end": v(-15.16, -10.6) * mm});
            skLineSegment(sketch, "E263", {"start": v(-15.16, -10.6) * mm, "end": v(-15.16, -11.44) * mm});
            skLineSegment(sketch, "E264", {"start": v(-15.16, -11.44) * mm, "end": v(-15.16, -12.28) * mm});
            skLineSegment(sketch, "E265", {"start": v(-15.16, -12.28) * mm, "end": v(-13.16, -12.28) * mm});
            skLineSegment(sketch, "E266", {"start": v(-13.16, -12.28) * mm, "end": v(-11.17, -12.28) * mm});
            skLineSegment(sketch, "E267", {"start": v(-11.17, -12.28) * mm, "end": v(-11.17, -13.56) * mm});
            skLineSegment(sketch, "E268", {"start": v(-11.17, -13.56) * mm, "end": v(-11.17, -14.84) * mm});
            skLineSegment(sketch, "E269", {"start": v(-11.17, -14.84) * mm, "end": v(-13.16, -14.84) * mm});
            skLineSegment(sketch, "E270", {"start": v(-13.16, -14.84) * mm, "end": v(-15.16, -14.84) * mm});
            skLineSegment(sketch, "E271", {"start": v(-15.16, -14.84) * mm, "end": v(-15.16, -15.84) * mm});
            skLineSegment(sketch, "E272", {"start": v(-15.16, -15.84) * mm, "end": v(-15.16, -16.84) * mm});
            skLineSegment(sketch, "E273", {"start": v(-15.16, -16.84) * mm, "end": v(-13.06, -16.84) * mm});
            skLineSegment(sketch, "E274", {"start": v(-13.06, -16.84) * mm, "end": v(-10.96, -16.84) * mm});
            skLineSegment(sketch, "E275", {"start": v(-10.96, -16.84) * mm, "end": v(-10.79, -17.88) * mm});
            skFitSpline(sketch, "E276", {"points": [v(-10.79, -17.88) * mm, v(-10.7, -18.45) * mm, v(-10.69, -19.03) * mm, v(-10.77, -19.16) * mm]});
            skFitSpline(sketch, "E277", {"points": [v(-10.77, -19.16) * mm, v(-10.94, -19.44) * mm, v(-18.1, -19.49) * mm, v(-18.38, -19.21) * mm]});
            skFitSpline(sketch, "E278", {"points": [v(-11.45, -18.27) * mm, v(-11.45, -17.77) * mm, v(-11.69, -17.7) * mm, v(-13.66, -17.63) * mm]});
            skLineSegment(sketch, "E279", {"start": v(-13.66, -17.63) * mm, "end": v(-15.87, -17.55) * mm});
            skLineSegment(sketch, "E280", {"start": v(-15.87, -17.55) * mm, "end": v(-15.87, -15.84) * mm});
            skLineSegment(sketch, "E281", {"start": v(-15.87, -15.84) * mm, "end": v(-15.87, -14.13) * mm});
            skLineSegment(sketch, "E282", {"start": v(-15.87, -14.13) * mm, "end": v(-13.95, -14.05) * mm});
            skFitSpline(sketch, "E283", {"points": [v(-13.95, -14.05) * mm, v(-12.26, -13.97) * mm, v(-12.02, -13.9) * mm, v(-12.02, -13.4) * mm]});
            skFitSpline(sketch, "E284", {"points": [v(-12.02, -13.4) * mm, v(-12.02, -12.9) * mm, v(-12.23, -12.85) * mm, v(-14.03, -12.85) * mm]});
            skLineSegment(sketch, "E285", {"start": v(-14.03, -12.85) * mm, "end": v(-16.04, -12.85) * mm});
            skLineSegment(sketch, "E286", {"start": v(-16.04, -12.85) * mm, "end": v(-15.95, -11.36) * mm});
            skLineSegment(sketch, "E287", {"start": v(-15.95, -11.36) * mm, "end": v(-15.87, -9.86) * mm});
            skLineSegment(sketch, "E288", {"start": v(-15.87, -9.86) * mm, "end": v(-13.8, -9.78) * mm});
            skFitSpline(sketch, "E289", {"points": [v(-13.8, -9.78) * mm, v(-11.97, -9.7) * mm, v(-11.74, -9.63) * mm, v(-11.74, -9.14) * mm]});
            skFitSpline(sketch, "E290", {"points": [v(-11.74, -9.14) * mm, v(-11.74, -8.62) * mm, v(-11.95, -8.58) * mm, v(-14.73, -8.58) * mm]});
            skLineSegment(sketch, "E291", {"start": v(-14.73, -8.58) * mm, "end": v(-17.72, -8.58) * mm});
            skLineSegment(sketch, "E292", {"start": v(-17.72, -8.58) * mm, "end": v(-17.72, -13.7) * mm});
            skLineSegment(sketch, "E293", {"start": v(-17.72, -13.7) * mm, "end": v(-17.72, -18.83) * mm});
            skLineSegment(sketch, "E294", {"start": v(-17.72, -18.83) * mm, "end": v(-14.59, -18.83) * mm});
            skFitSpline(sketch, "E295", {"points": [v(-14.59, -18.83) * mm, v(-11.67, -18.83) * mm, v(-11.45, -18.8) * mm, v(-11.45, -18.27) * mm]});
            skFitSpline(sketch, "E296", {"points": [v(0.14, -19.22) * mm, v(0.03, -19.11) * mm, v(-0.06, -16.62) * mm, v(-0.06, -13.7) * mm]});
            skFitSpline(sketch, "E297", {"points": [v(-0.06, -13.7) * mm, v(-0.06, -9.76) * mm, v(0.03, -8.29) * mm, v(0.3, -8.07) * mm]});
            skFitSpline(sketch, "E298", {"points": [v(0.3, -8.07) * mm, v(0.7, -7.73) * mm, v(2.73, -7.84) * mm, v(3.12, -8.23) * mm]});
            skFitSpline(sketch, "E299", {"points": [v(3.12, -8.23) * mm, v(3.26, -8.36) * mm, v(3.33, -10.9) * mm, v(3.3, -13.87) * mm]});
            skLineSegment(sketch, "E300", {"start": v(3.3, -13.87) * mm, "end": v(3.21, -19.26) * mm});
            skLineSegment(sketch, "E301", {"start": v(3.21, -19.26) * mm, "end": v(1.78, -19.34) * mm});
            skFitSpline(sketch, "E302", {"points": [v(1.78, -19.34) * mm, v(0.99, -19.39) * mm, v(0.25, -19.33) * mm, v(0.14, -19.22) * mm]});
            skLineSegment(sketch, "E303", {"start": v(2.5, -13.7) * mm, "end": v(2.5, -8.58) * mm});
            skLineSegment(sketch, "E304", {"start": v(2.5, -8.58) * mm, "end": v(1.65, -8.58) * mm});
            skLineSegment(sketch, "E305", {"start": v(1.65, -8.58) * mm, "end": v(0.8, -8.58) * mm});
            skLineSegment(sketch, "E306", {"start": v(0.8, -8.58) * mm, "end": v(0.8, -13.7) * mm});
            skLineSegment(sketch, "E307", {"start": v(0.8, -13.7) * mm, "end": v(0.8, -18.83) * mm});
            skLineSegment(sketch, "E308", {"start": v(0.8, -18.83) * mm, "end": v(1.65, -18.83) * mm});
            skLineSegment(sketch, "E309", {"start": v(1.65, -18.83) * mm, "end": v(2.5, -18.83) * mm});
            skLineSegment(sketch, "E310", {"start": v(2.5, -18.83) * mm, "end": v(2.5, -13.7) * mm});
            skFitSpline(sketch, "E311", {"points": [v(4.5, -19.16) * mm, v(4.5, -18.63) * mm, v(7.68, -8.43) * mm, v(7.95, -8.1) * mm]});
            skFitSpline(sketch, "E312", {"points": [v(7.95, -8.1) * mm, v(8.26, -7.73) * mm, v(11.23, -7.8) * mm, v(11.6, -8.18) * mm]});
            skFitSpline(sketch, "E313", {"points": [v(11.6, -8.18) * mm, v(11.88, -8.47) * mm, v(15.03, -18.46) * mm, v(15.03, -19.05) * mm]});
            skFitSpline(sketch, "E314", {"points": [v(15.03, -19.05) * mm, v(15.03, -19.33) * mm, v(14.62, -19.4) * mm, v(13.43, -19.34) * mm]});
            skLineSegment(sketch, "E315", {"start": v(13.43, -19.34) * mm, "end": v(11.83, -19.26) * mm});
            skLineSegment(sketch, "E316", {"start": v(11.83, -19.26) * mm, "end": v(11.36, -17.98) * mm});
            skFitSpline(sketch, "E317", {"points": [v(11.36, -17.98) * mm, v(10.92, -16.76) * mm, v(10.83, -16.7) * mm, v(9.7, -16.6) * mm]});
            skLineSegment(sketch, "E318", {"start": v(9.7, -16.6) * mm, "end": v(8.5, -16.52) * mm});
            skLineSegment(sketch, "E319", {"start": v(8.5, -16.52) * mm, "end": v(8.11, -17.89) * mm});
            skLineSegment(sketch, "E320", {"start": v(8.11, -17.89) * mm, "end": v(7.71, -19.26) * mm});
            skLineSegment(sketch, "E321", {"start": v(7.71, -19.26) * mm, "end": v(6.1, -19.34) * mm});
            skFitSpline(sketch, "E322", {"points": [v(6.1, -19.34) * mm, v(5.2, -19.4) * mm, v(4.5, -19.3) * mm, v(4.5, -19.16) * mm]});
            skFitSpline(sketch, "E323", {"points": [v(7.16, -18.33) * mm, v(7.24, -18.06) * mm, v(7.39, -17.41) * mm, v(7.49, -16.9) * mm]});
            skLineSegment(sketch, "E324", {"start": v(7.49, -16.9) * mm, "end": v(7.68, -15.96) * mm});
            skLineSegment(sketch, "E325", {"start": v(7.68, -15.96) * mm, "end": v(9.69, -16.04) * mm});
            skLineSegment(sketch, "E326", {"start": v(9.69, -16.04) * mm, "end": v(11.7, -16.13) * mm});
            skLineSegment(sketch, "E327", {"start": v(11.7, -16.13) * mm, "end": v(12.1, -17.48) * mm});
            skFitSpline(sketch, "E328", {"points": [v(12.1, -17.48) * mm, v(12.45, -18.7) * mm, v(12.57, -18.83) * mm, v(13.33, -18.83) * mm]});
            skFitSpline(sketch, "E329", {"points": [v(13.33, -18.83) * mm, v(13.8, -18.83) * mm, v(14.18, -18.79) * mm, v(14.18, -18.74) * mm]});
            skFitSpline(sketch, "E330", {"points": [v(14.18, -18.74) * mm, v(14.18, -18.69) * mm, v(13.81, -17.5) * mm, v(13.37, -16.1) * mm]});
            skFitSpline(sketch, "E331", {"points": [v(13.37, -16.1) * mm, v(12.92, -14.7) * mm, v(12.27, -12.6) * mm, v(11.92, -11.43) * mm]});
            skFitSpline(sketch, "E332", {"points": [v(11.92, -11.43) * mm, v(11.56, -10.25) * mm, v(11.23, -9.13) * mm, v(11.17, -8.93) * mm]});
            skFitSpline(sketch, "E333", {"points": [v(11.17, -8.93) * mm, v(11.1, -8.72) * mm, v(10.56, -8.58) * mm, v(9.79, -8.58) * mm]});
            skLineSegment(sketch, "E334", {"start": v(9.79, -8.58) * mm, "end": v(8.52, -8.58) * mm});
            skLineSegment(sketch, "E335", {"start": v(8.52, -8.58) * mm, "end": v(7.75, -11.07) * mm});
            skFitSpline(sketch, "E336", {"points": [v(7.75, -11.07) * mm, v(7.33, -12.44) * mm, v(6.64, -14.75) * mm, v(6.2, -16.2) * mm]});
            skLineSegment(sketch, "E337", {"start": v(6.2, -16.2) * mm, "end": v(5.4, -18.83) * mm});
            skLineSegment(sketch, "E338", {"start": v(5.4, -18.83) * mm, "end": v(6.21, -18.83) * mm});
            skFitSpline(sketch, "E339", {"points": [v(6.21, -18.83) * mm, v(6.74, -18.83) * mm, v(7.07, -18.66) * mm, v(7.16, -18.33) * mm]});
            skFitSpline(sketch, "E340", {"points": [v(8.22, -14.2) * mm, v(8.27, -12.83) * mm, v(9.2, -10.15) * mm, v(9.66, -10.06) * mm]});
            skFitSpline(sketch, "E341", {"points": [v(9.66, -10.06) * mm, v(10.02, -10) * mm, v(10.26, -10.48) * mm, v(10.73, -12.21) * mm]});
            skFitSpline(sketch, "E342", {"points": [v(10.73, -12.21) * mm, v(11.06, -13.45) * mm, v(11.33, -14.54) * mm, v(11.33, -14.65) * mm]});
            skFitSpline(sketch, "E343", {"points": [v(11.33, -14.65) * mm, v(11.33, -14.76) * mm, v(10.63, -14.84) * mm, v(9.76, -14.84) * mm]});
            skFitSpline(sketch, "E344", {"points": [v(9.76, -14.84) * mm, v(8.32, -14.84) * mm, v(8.2, -14.8) * mm, v(8.22, -14.2) * mm]});
            skFitSpline(sketch, "E345", {"points": [v(10.47, -14.2) * mm, v(10.47, -14.16) * mm, v(10.3, -13.56) * mm, v(10.08, -12.85) * mm]});
            skLineSegment(sketch, "E346", {"start": v(10.08, -12.85) * mm, "end": v(9.7, -11.57) * mm});
            skLineSegment(sketch, "E347", {"start": v(9.7, -11.57) * mm, "end": v(9.37, -12.7) * mm});
            skFitSpline(sketch, "E348", {"points": [v(9.37, -12.7) * mm, v(8.94, -14.25) * mm, v(8.95, -14.27) * mm, v(9.76, -14.27) * mm]});
            skFitSpline(sketch, "E349", {"points": [v(9.76, -14.27) * mm, v(10.16, -14.27) * mm, v(10.47, -14.24) * mm, v(10.47, -14.2) * mm]});
            skLineSegment(sketch, "E350", {"start": v(16.52, -13.64) * mm, "end": v(16.6, -7.88) * mm});
            skLineSegment(sketch, "E351", {"start": v(16.6, -7.88) * mm, "end": v(18.08, -7.85) * mm});
            skFitSpline(sketch, "E352", {"points": [v(18.08, -7.85) * mm, v(18.9, -7.83) * mm, v(19.67, -7.9) * mm, v(19.8, -7.98) * mm]});
            skFitSpline(sketch, "E353", {"points": [v(19.8, -7.98) * mm, v(19.95, -8.08) * mm, v(20.78, -9.43) * mm, v(21.67, -11) * mm]});
            skLineSegment(sketch, "E354", {"start": v(21.67, -11) * mm, "end": v(23.29, -13.85) * mm});
            skLineSegment(sketch, "E355", {"start": v(23.29, -13.85) * mm, "end": v(23.29, -10.95) * mm});
            skFitSpline(sketch, "E356", {"points": [v(23.29, -10.95) * mm, v(23.3, -7.75) * mm, v(23.33, -7.7) * mm, v(25.36, -7.97) * mm]});
            skLineSegment(sketch, "E357", {"start": v(25.36, -7.97) * mm, "end": v(26.14, -8.07) * mm});
            skLineSegment(sketch, "E358", {"start": v(26.14, -8.07) * mm, "end": v(26.14, -13.74) * mm});
            skLineSegment(sketch, "E359", {"start": v(26.14, -13.74) * mm, "end": v(26.14, -19.4) * mm});
            skLineSegment(sketch, "E360", {"start": v(26.14, -19.4) * mm, "end": v(24.6, -19.4) * mm});
            skFitSpline(sketch, "E361", {"points": [v(24.6, -19.4) * mm, v(23.73, -19.4) * mm, v(22.95, -19.25) * mm, v(22.78, -19.04) * mm]});
            skFitSpline(sketch, "E362", {"points": [v(22.78, -19.04) * mm, v(22.62, -18.85) * mm, v(21.78, -17.34) * mm, v(20.9, -15.7) * mm]});
            skLineSegment(sketch, "E363", {"start": v(20.9, -15.7) * mm, "end": v(19.31, -12.7) * mm});
            skLineSegment(sketch, "E364", {"start": v(19.31, -12.7) * mm, "end": v(19.3, -16.05) * mm});
            skLineSegment(sketch, "E365", {"start": v(19.3, -16.05) * mm, "end": v(19.3, -19.4) * mm});
            skLineSegment(sketch, "E366", {"start": v(19.3, -19.4) * mm, "end": v(17.87, -19.4) * mm});
            skLineSegment(sketch, "E367", {"start": v(17.87, -19.4) * mm, "end": v(16.44, -19.4) * mm});
            skLineSegment(sketch, "E368", {"start": v(16.44, -19.4) * mm, "end": v(16.52, -13.64) * mm});
            skLineSegment(sketch, "E369", {"start": v(16.52, -13.64) * mm, "end": v(16.52, -13.64) * mm});
            skFitSpline(sketch, "E370", {"points": [v(18.51, -14.92) * mm, v(18.58, -11.62) * mm, v(18.66, -11) * mm, v(19.04, -10.92) * mm]});
            skFitSpline(sketch, "E371", {"points": [v(19.04, -10.92) * mm, v(19.34, -10.86) * mm, v(19.64, -11.21) * mm, v(19.93, -11.94) * mm]});
            skFitSpline(sketch, "E372", {"points": [v(19.93, -11.94) * mm, v(20.17, -12.55) * mm, v(21.1, -14.35) * mm, v(21.99, -15.94) * mm]});
            skFitSpline(sketch, "E373", {"points": [v(21.99, -15.94) * mm, v(23.55, -18.73) * mm, v(23.64, -18.83) * mm, v(24.59, -18.83) * mm]});
            skLineSegment(sketch, "E374", {"start": v(24.59, -18.83) * mm, "end": v(25.57, -18.83) * mm});
            skLineSegment(sketch, "E375", {"start": v(25.57, -18.83) * mm, "end": v(25.57, -13.7) * mm});
            skLineSegment(sketch, "E376", {"start": v(25.57, -13.7) * mm, "end": v(25.57, -8.58) * mm});
            skLineSegment(sketch, "E377", {"start": v(25.57, -8.58) * mm, "end": v(24.86, -8.58) * mm});
            skLineSegment(sketch, "E378", {"start": v(24.86, -8.58) * mm, "end": v(24.15, -8.58) * mm});
            skLineSegment(sketch, "E379", {"start": v(24.15, -8.58) * mm, "end": v(24.15, -12.25) * mm});
            skFitSpline(sketch, "E380", {"points": [v(24.15, -12.25) * mm, v(24.15, -16.75) * mm, v(23.84, -17.13) * mm, v(22.45, -14.32) * mm]});
            skFitSpline(sketch, "E381", {"points": [v(22.45, -14.32) * mm, v(21.94, -13.28) * mm, v(21.02, -11.56) * mm, v(20.4, -10.5) * mm]});
            skFitSpline(sketch, "E382", {"points": [v(20.4, -10.5) * mm, v(19.31, -8.64) * mm, v(19.24, -8.58) * mm, v(18.15, -8.58) * mm]});
            skLineSegment(sketch, "E383", {"start": v(18.15, -8.58) * mm, "end": v(17.03, -8.58) * mm});
            skLineSegment(sketch, "E384", {"start": v(17.03, -8.58) * mm, "end": v(17.03, -13.7) * mm});
            skLineSegment(sketch, "E385", {"start": v(17.03, -13.7) * mm, "end": v(17.03, -18.83) * mm});
            skLineSegment(sketch, "E386", {"start": v(17.03, -18.83) * mm, "end": v(17.73, -18.83) * mm});
            skLineSegment(sketch, "E387", {"start": v(17.73, -18.83) * mm, "end": v(18.43, -18.83) * mm});
            skLineSegment(sketch, "E388", {"start": v(18.43, -18.83) * mm, "end": v(18.51, -14.92) * mm});
            skLineSegment(sketch, "E389", {"start": v(-9.46, 8.14) * mm, "end": v(-9.46, 13.47) * mm});
            skLineSegment(sketch, "E390", {"start": v(-9.46, 13.47) * mm, "end": v(-11.17, 11.79) * mm});
            skLineSegment(sketch, "E391", {"start": v(-11.17, 11.79) * mm, "end": v(-12.87, 10.1) * mm});
            skLineSegment(sketch, "E392", {"start": v(-12.87, 10.1) * mm, "end": v(-14.16, 11.36) * mm});
            skFitSpline(sketch, "E393", {"points": [v(-14.16, 11.36) * mm, v(-14.86, 12.05) * mm, v(-15.44, 12.75) * mm, v(-15.44, 12.9) * mm]});
            skFitSpline(sketch, "E394", {"points": [v(-15.44, 12.9) * mm, v(-15.44, 13.07) * mm, v(-12.01, 16.63) * mm, v(-7.82, 20.82) * mm]});
            skFitSpline(sketch, "E395", {"points": [v(-7.82, 20.82) * mm, v(-3.06, 25.6) * mm, v(-0.4, 28.44) * mm, v(-0.73, 28.44) * mm]});
            skFitSpline(sketch, "E396", {"points": [v(-0.73, 28.44) * mm, v(-1.01, 28.44) * mm, v(-1.62, 28.82) * mm, v(-2.08, 29.28) * mm]});
            skFitSpline(sketch, "E397", {"points": [v(-2.08, 29.28) * mm, v(-3.88, 31.08) * mm, v(-2.58, 34.42) * mm, v(-0.06, 34.42) * mm]});
            skFitSpline(sketch, "E398", {"points": [v(-0.06, 34.42) * mm, v(0.77, 34.42) * mm, v(2.14, 33.67) * mm, v(2.5, 33.02) * mm]});
            skFitSpline(sketch, "E399", {"points": [v(2.5, 33.02) * mm, v(2.87, 32.3) * mm, v(2.87, 30.55) * mm, v(2.48, 29.83) * mm]});
            skFitSpline(sketch, "E400", {"points": [v(2.48, 29.83) * mm, v(2.32, 29.52) * mm, v(1.8, 29.04) * mm, v(1.36, 28.77) * mm]});
            skLineSegment(sketch, "E401", {"start": v(1.36, 28.77) * mm, "end": v(0.53, 28.27) * mm});
            skLineSegment(sketch, "E402", {"start": v(0.53, 28.27) * mm, "end": v(3.32, 25.49) * mm});
            skFitSpline(sketch, "E403", {"points": [v(3.32, 25.49) * mm, v(5.82, 23) * mm, v(6.1, 22.8) * mm, v(5.99, 23.55) * mm]});
            skFitSpline(sketch, "E404", {"points": [v(5.99, 23.55) * mm, v(5.82, 24.67) * mm, v(6.58, 26.05) * mm, v(7.67, 26.61) * mm]});
            skFitSpline(sketch, "E405", {"points": [v(7.67, 26.61) * mm, v(8.88, 27.24) * mm, v(10.25, 26.94) * mm, v(11.17, 25.85) * mm]});
            skFitSpline(sketch, "E406", {"points": [v(11.17, 25.85) * mm, v(12.93, 23.75) * mm, v(11.2, 20.7) * mm, v(8.46, 21.1) * mm]});
            skFitSpline(sketch, "E407", {"points": [v(8.46, 21.1) * mm, v(7.68, 21.22) * mm, v(8, 20.82) * mm, v(11.45, 17.36) * mm]});
            skFitSpline(sketch, "E408", {"points": [v(11.45, 17.36) * mm, v(14.04, 14.77) * mm, v(15.32, 13.28) * mm, v(15.32, 12.87) * mm]});
            skFitSpline(sketch, "E409", {"points": [v(15.32, 12.87) * mm, v(15.32, 12.48) * mm, v(14.83, 11.85) * mm, v(14.02, 11.19) * mm]});
            skLineSegment(sketch, "E410", {"start": v(14.02, 11.19) * mm, "end": v(12.72, 10.12) * mm});
            skLineSegment(sketch, "E411", {"start": v(12.72, 10.12) * mm, "end": v(11.03, 11.8) * mm});
            skLineSegment(sketch, "E412", {"start": v(11.03, 11.8) * mm, "end": v(9.34, 13.47) * mm});
            skLineSegment(sketch, "E413", {"start": v(9.34, 13.47) * mm, "end": v(9.34, 8.13) * mm});
            skLineSegment(sketch, "E414", {"start": v(9.34, 8.13) * mm, "end": v(9.34, 2.79) * mm});
            skLineSegment(sketch, "E415", {"start": v(9.34, 2.79) * mm, "end": v(7.27, 2.87) * mm});
            skLineSegment(sketch, "E416", {"start": v(7.27, 2.87) * mm, "end": v(5.2, 2.96) * mm});
            skLineSegment(sketch, "E417", {"start": v(5.2, 2.96) * mm, "end": v(5.18, 10.32) * mm});
            skLineSegment(sketch, "E418", {"start": v(5.18, 10.32) * mm, "end": v(5.14, 17.68) * mm});
            skLineSegment(sketch, "E419", {"start": v(5.14, 17.68) * mm, "end": v(3.54, 19.28) * mm});
            skLineSegment(sketch, "E420", {"start": v(3.54, 19.28) * mm, "end": v(1.93, 20.9) * mm});
            skLineSegment(sketch, "E421", {"start": v(1.93, 20.9) * mm, "end": v(1.93, 11.85) * mm});
            skLineSegment(sketch, "E422", {"start": v(1.93, 11.85) * mm, "end": v(1.93, 2.81) * mm});
            skLineSegment(sketch, "E423", {"start": v(1.93, 2.81) * mm, "end": v(-0.06, 2.81) * mm});
            skLineSegment(sketch, "E424", {"start": v(-0.06, 2.81) * mm, "end": v(-2.06, 2.81) * mm});
            skLineSegment(sketch, "E425", {"start": v(-2.06, 2.81) * mm, "end": v(-2.06, 11.79) * mm});
            skLineSegment(sketch, "E426", {"start": v(-2.06, 11.79) * mm, "end": v(-2.06, 20.76) * mm});
            skLineSegment(sketch, "E427", {"start": v(-2.06, 20.76) * mm, "end": v(-3.62, 19.28) * mm});
            skLineSegment(sketch, "E428", {"start": v(-3.62, 19.28) * mm, "end": v(-5.19, 17.8) * mm});
            skLineSegment(sketch, "E429", {"start": v(-5.19, 17.8) * mm, "end": v(-5.19, 10.3) * mm});
            skLineSegment(sketch, "E430", {"start": v(-5.19, 10.3) * mm, "end": v(-5.19, 2.81) * mm});
            skLineSegment(sketch, "E431", {"start": v(-5.19, 2.81) * mm, "end": v(-7.32, 2.81) * mm});
            skLineSegment(sketch, "E432", {"start": v(-7.32, 2.81) * mm, "end": v(-9.46, 2.81) * mm});
            skLineSegment(sketch, "E433", {"start": v(-9.46, 2.81) * mm, "end": v(-9.46, 8.14) * mm});
            skLineSegment(sketch, "E434", {"start": v(-5.76, 10.72) * mm, "end": v(-5.76, 18.07) * mm});
            skLineSegment(sketch, "E435", {"start": v(-5.76, 18.07) * mm, "end": v(-4.11, 19.7) * mm});
            skFitSpline(sketch, "E436", {"points": [v(-4.11, 19.7) * mm, v(-1.37, 22.4) * mm, v(-1.49, 22.73) * mm, v(-1.49, 12.35) * mm]});
            skLineSegment(sketch, "E437", {"start": v(-1.49, 12.35) * mm, "end": v(-1.49, 3.38) * mm});
            skLineSegment(sketch, "E438", {"start": v(-1.49, 3.38) * mm, "end": v(-0.06, 3.38) * mm});
            skLineSegment(sketch, "E439", {"start": v(-0.06, 3.38) * mm, "end": v(1.36, 3.38) * mm});
            skLineSegment(sketch, "E440", {"start": v(1.36, 3.38) * mm, "end": v(1.36, 12.34) * mm});
            skFitSpline(sketch, "E441", {"points": [v(1.36, 12.34) * mm, v(1.36, 18.76) * mm, v(1.45, 21.35) * mm, v(1.69, 21.5) * mm]});
            skFitSpline(sketch, "E442", {"points": [v(1.69, 21.5) * mm, v(1.88, 21.61) * mm, v(2.8, 20.88) * mm, v(3.97, 19.7) * mm]});
            skLineSegment(sketch, "E443", {"start": v(3.97, 19.7) * mm, "end": v(5.92, 17.69) * mm});
            skLineSegment(sketch, "E444", {"start": v(5.92, 17.69) * mm, "end": v(5.92, 10.54) * mm});
            skLineSegment(sketch, "E445", {"start": v(5.92, 10.54) * mm, "end": v(5.92, 3.38) * mm});
            skLineSegment(sketch, "E446", {"start": v(5.92, 3.38) * mm, "end": v(7.34, 3.38) * mm});
            skLineSegment(sketch, "E447", {"start": v(7.34, 3.38) * mm, "end": v(8.77, 3.38) * mm});
            skLineSegment(sketch, "E448", {"start": v(8.77, 3.38) * mm, "end": v(8.77, 8.8) * mm});
            skFitSpline(sketch, "E449", {"points": [v(8.77, 8.8) * mm, v(8.77, 12.86) * mm, v(8.85, 14.2) * mm, v(9.11, 14.2) * mm]});
            skFitSpline(sketch, "E450", {"points": [v(9.11, 14.2) * mm, v(9.3, 14.2) * mm, v(10.2, 13.48) * mm, v(11.09, 12.6) * mm]});
            skLineSegment(sketch, "E451", {"start": v(11.09, 12.6) * mm, "end": v(12.72, 10.98) * mm});
            skLineSegment(sketch, "E452", {"start": v(12.72, 10.98) * mm, "end": v(13.71, 11.81) * mm});
            skFitSpline(sketch, "E453", {"points": [v(13.71, 11.81) * mm, v(14.26, 12.27) * mm, v(14.72, 12.77) * mm, v(14.73, 12.93) * mm]});
            skFitSpline(sketch, "E454", {"points": [v(14.73, 12.93) * mm, v(14.74, 13.08) * mm, v(11.45, 16.51) * mm, v(7.41, 20.54) * mm]});
            skLineSegment(sketch, "E455", {"start": v(7.41, 20.54) * mm, "end": v(0.08, 27.87) * mm});
            skLineSegment(sketch, "E456", {"start": v(0.08, 27.87) * mm, "end": v(-7.4, 20.39) * mm});
            skLineSegment(sketch, "E457", {"start": v(-7.4, 20.39) * mm, "end": v(-14.88, 12.9) * mm});
            skLineSegment(sketch, "E458", {"start": v(-14.88, 12.9) * mm, "end": v(-13.88, 11.93) * mm});
            skLineSegment(sketch, "E459", {"start": v(-13.88, 11.93) * mm, "end": v(-12.87, 10.95) * mm});
            skLineSegment(sketch, "E460", {"start": v(-12.87, 10.95) * mm, "end": v(-11.2, 12.61) * mm});
            skFitSpline(sketch, "E461", {"points": [v(-11.2, 12.61) * mm, v(-10.26, 13.54) * mm, v(-9.38, 14.19) * mm, v(-9.2, 14.08) * mm]});
            skFitSpline(sketch, "E462", {"points": [v(-9.2, 14.08) * mm, v(-9, 13.95) * mm, v(-8.9, 12.14) * mm, v(-8.9, 8.63) * mm]});
            skLineSegment(sketch, "E463", {"start": v(-8.9, 8.63) * mm, "end": v(-8.9, 3.38) * mm});
            skLineSegment(sketch, "E464", {"start": v(-8.9, 3.38) * mm, "end": v(-7.32, 3.38) * mm});
            skLineSegment(sketch, "E465", {"start": v(-7.32, 3.38) * mm, "end": v(-5.76, 3.38) * mm});
            skLineSegment(sketch, "E466", {"start": v(-5.76, 3.38) * mm, "end": v(-5.76, 10.72) * mm});
            skFitSpline(sketch, "E467", {"points": [v(10.7, 22.39) * mm, v(11.7, 23.74) * mm, v(11.3, 25.4) * mm, v(9.84, 26.1) * mm]});
            skFitSpline(sketch, "E468", {"points": [v(9.84, 26.1) * mm, v(8.8, 26.6) * mm, v(7.17, 25.94) * mm, v(6.76, 24.86) * mm]});
            skFitSpline(sketch, "E469", {"points": [v(6.76, 24.86) * mm, v(6.38, 23.85) * mm, v(6.86, 22.37) * mm, v(7.7, 21.94) * mm]});
            skFitSpline(sketch, "E470", {"points": [v(7.7, 21.94) * mm, v(8.56, 21.51) * mm, v(10.24, 21.76) * mm, v(10.7, 22.39) * mm]});
            skFitSpline(sketch, "E471", {"points": [v(1.47, 29.6) * mm, v(2.04, 30.06) * mm, v(2.22, 30.45) * mm, v(2.22, 31.28) * mm]});
            skFitSpline(sketch, "E472", {"points": [v(2.22, 31.28) * mm, v(2.22, 33.5) * mm, v(0.2, 34.52) * mm, v(-1.43, 33.14) * mm]});
            skFitSpline(sketch, "E473", {"points": [v(-1.43, 33.14) * mm, v(-3.84, 31.11) * mm, v(-1, 27.66) * mm, v(1.47, 29.6) * mm]});
            skFitSpline(sketch, "E474", {"points": [v(-10.51, 21.38) * mm, v(-11.41, 21.82) * mm, v(-12.11, 23.45) * mm, v(-11.9, 24.6) * mm]});
            skFitSpline(sketch, "E475", {"points": [v(-11.9, 24.6) * mm, v(-11.66, 25.9) * mm, v(-10.3, 27.02) * mm, v(-8.98, 27.02) * mm]});
            skFitSpline(sketch, "E476", {"points": [v(-8.98, 27.02) * mm, v(-7.54, 27.02) * mm, v(-6.04, 25.5) * mm, v(-6.04, 24.03) * mm]});
            skFitSpline(sketch, "E477", {"points": [v(-6.04, 24.03) * mm, v(-6.04, 23.21) * mm, v(-6.26, 22.76) * mm, v(-7.01, 22) * mm]});
            skFitSpline(sketch, "E478", {"points": [v(-7.01, 22) * mm, v(-8.04, 20.98) * mm, v(-9.24, 20.76) * mm, v(-10.51, 21.38) * mm]});
            skFitSpline(sketch, "E479", {"points": [v(-7.94, 21.93) * mm, v(-6.56, 22.55) * mm, v(-6.24, 24.28) * mm, v(-7.29, 25.5) * mm]});
            skFitSpline(sketch, "E480", {"points": [v(-7.29, 25.5) * mm, v(-7.8, 26.08) * mm, v(-8.22, 26.28) * mm, v(-9, 26.28) * mm]});
            skFitSpline(sketch, "E481", {"points": [v(-9, 26.28) * mm, v(-11.18, 26.28) * mm, v(-12.15, 23.7) * mm, v(-10.5, 22.28) * mm]});
            skFitSpline(sketch, "E482", {"points": [v(-10.5, 22.28) * mm, v(-9.63, 21.54) * mm, v(-8.98, 21.45) * mm, v(-7.94, 21.93) * mm]});
            skLineSegment(sketch, "E483.bottom", {"start": v(55.5, 37.95) * mm, "end": v(-55.5, 37.95) * mm});
            skLineSegment(sketch, "E483.top", {"start": v(55.5, -37.95) * mm, "end": v(-55.5, -37.95) * mm});
            skLineSegment(sketch, "E483.left", {"start": v(55.5, 37.95) * mm, "end": v(55.5, -37.95) * mm});
            skLineSegment(sketch, "E483.right", {"start": v(-55.5, 37.95) * mm, "end": v(-55.5, -37.95) * mm});
            skPoint(sketch, "E483.middle", {"position": v(0, 0) * mm});
            skFitSpline(sketch, "E484", {"points": [v(-14.02, -30.93) * mm, v(-13.42, -31.25) * mm, v(-12.75, -30.78) * mm, v(-13.59, -29.68) * mm, v(-14.02, -30.93) * mm]});
            skFitSpline(sketch, "E485", {"points": [v(-3.1, -31.35) * mm, v(-3.58, -30.87) * mm, v(-3.1, -29.95) * mm, v(-2.7, -30.87) * mm, v(-3.1, -31.35) * mm]});
            skSolve(sketch);
        }
        {
            var Q0;
            Q0=qCreatedBy(makeId("Top.planeOp"),FACE);
            var sketch = newSketch(context, id + "F1", { "sketchPlane" : qUnion([Q0])});
            skLineSegment(sketch, "E486.bottom", {"start": v(-55.5, 37.95) * mm, "end": v(55.5, 37.95) * mm});
            skLineSegment(sketch, "E486.top", {"start": v(-55.5, -37.95) * mm, "end": v(55.5, -37.95) * mm});
            skLineSegment(sketch, "E486.left", {"start": v(-55.5, 37.95) * mm, "end": v(-55.5, -37.95) * mm});
            skLineSegment(sketch, "E486.right", {"start": v(55.5, 37.95) * mm, "end": v(55.5, -37.95) * mm});
            skSolve(sketch);
        }
        {
            var Q0;
            Q0=qSketchRegion(id+"F1",true);
            extrude(context, id + "F2", {"entities" : qUnion([Q0]), "depth" : 1 * mm});
        }
        {
            var Q0;
            Q0=makeQuery(id+"F0.imprint","IMPRINT",FACE,{"disambiguationData":[TD([[makeQuery(id+"F0.imprint","IMPRINT",EDGE,{"derivedFrom":sQuery(id+"F0.wireOp",EDGE,"E0")}),1.0]])]});
            var Q1;
            Q1=makeQuery(id+"F0.imprint","IMPRINT",FACE,{"disambiguationData":[TD([[makeQuery(id+"F0.imprint","IMPRINT",EDGE,{"derivedFrom":sQuery(id+"F0.wireOp",EDGE,"E228")}),-1.0]])]});
            var Q2;
            Q2=makeQuery(id+"F0.imprint","IMPRINT",FACE,{"disambiguationData":[TD([[makeQuery(id+"F0.imprint","IMPRINT",EDGE,{"derivedFrom":sQuery(id+"F0.wireOp",EDGE,"E232")}),1.0]])]});
            var Q3;
            Q3=makeQuery(id+"F0.imprint","IMPRINT",FACE,{"disambiguationData":[TD([[makeQuery(id+"F0.imprint","IMPRINT",EDGE,{"derivedFrom":sQuery(id+"F0.wireOp",EDGE,"E345")}),1.0]])]});
            var Q4;
            Q4=makeQuery(id+"F0.imprint","IMPRINT",FACE,{"disambiguationData":[TD([[makeQuery(id+"F0.imprint","IMPRINT",EDGE,{"derivedFrom":sQuery(id+"F0.wireOp",EDGE,"E340")}),-1.0]])]});
            var Q5;
            Q5=makeQuery(id+"F0.imprint","IMPRINT",FACE,{"disambiguationData":[TD([[makeQuery(id+"F0.imprint","IMPRINT",EDGE,{"derivedFrom":sQuery(id+"F0.wireOp",EDGE,"E172")}),1.0]])]});
            var Q6;
            Q6=makeQuery(id+"F0.imprint","IMPRINT",FACE,{"disambiguationData":[TD([[makeQuery(id+"F0.imprint","IMPRINT",EDGE,{"derivedFrom":sQuery(id+"F0.wireOp",EDGE,"E166")}),-1.0]])]});
            var Q7;
            Q7=makeQuery(id+"F0.imprint","IMPRINT",FACE,{"disambiguationData":[TD([[makeQuery(id+"F0.imprint","IMPRINT",EDGE,{"derivedFrom":sQuery(id+"F0.wireOp",EDGE,"E54")}),1.0]])]});
            var Q8;
            Q8=makeQuery(id+"F0.imprint","IMPRINT",FACE,{"disambiguationData":[TD([[makeQuery(id+"F0.imprint","IMPRINT",EDGE,{"derivedFrom":sQuery(id+"F0.wireOp",EDGE,"E81")}),1.0]])]});
            var Q9;
            Q9=makeQuery(id+"F0.imprint","IMPRINT",FACE,{"disambiguationData":[TD([[makeQuery(id+"F0.imprint","IMPRINT",EDGE,{"derivedFrom":sQuery(id+"F0.wireOp",EDGE,"E100")}),1.0]])]});
            var Q10;
            Q10=makeQuery(id+"F0.imprint","IMPRINT",FACE,{"disambiguationData":[TD([[makeQuery(id+"F0.imprint","IMPRINT",EDGE,{"derivedFrom":sQuery(id+"F0.wireOp",EDGE,"b21fcf35-48a5-4af7-b02d-cd25d2a26831")}),1.0]])]});
            var Q11;
            Q11=makeQuery(id+"F0.imprint","IMPRINT",FACE,{"disambiguationData":[TD([[makeQuery(id+"F0.imprint","IMPRINT",EDGE,{"derivedFrom":sQuery(id+"F0.wireOp",EDGE,"E484")}),1.0]])]});
            var Q12;
            Q12=makeQuery(id+"F0.imprint","IMPRINT",FACE,{"disambiguationData":[TD([[makeQuery(id+"F0.imprint","IMPRINT",EDGE,{"derivedFrom":sQuery(id+"F0.wireOp",EDGE,"d2ea1035-2816-4439-82fa-66500c4e4ea2")}),1.0]])]});
            var Q13;
            Q13=makeQuery(id+"F0.imprint","IMPRINT",FACE,{"disambiguationData":[TD([[makeQuery(id+"F0.imprint","IMPRINT",EDGE,{"derivedFrom":sQuery(id+"F0.wireOp",EDGE,"E485")}),-1.0]])]});
            extrude(context, id + "F3", {"entities" : qUnion([Q0, Q1, Q2, Q3, Q4, Q5, Q6, Q7, Q8, Q9, Q10, Q11, Q12, Q13]), "operationType" : NewBodyOperationType.ADD, "depth" : 3 * mm});
        }
    });
